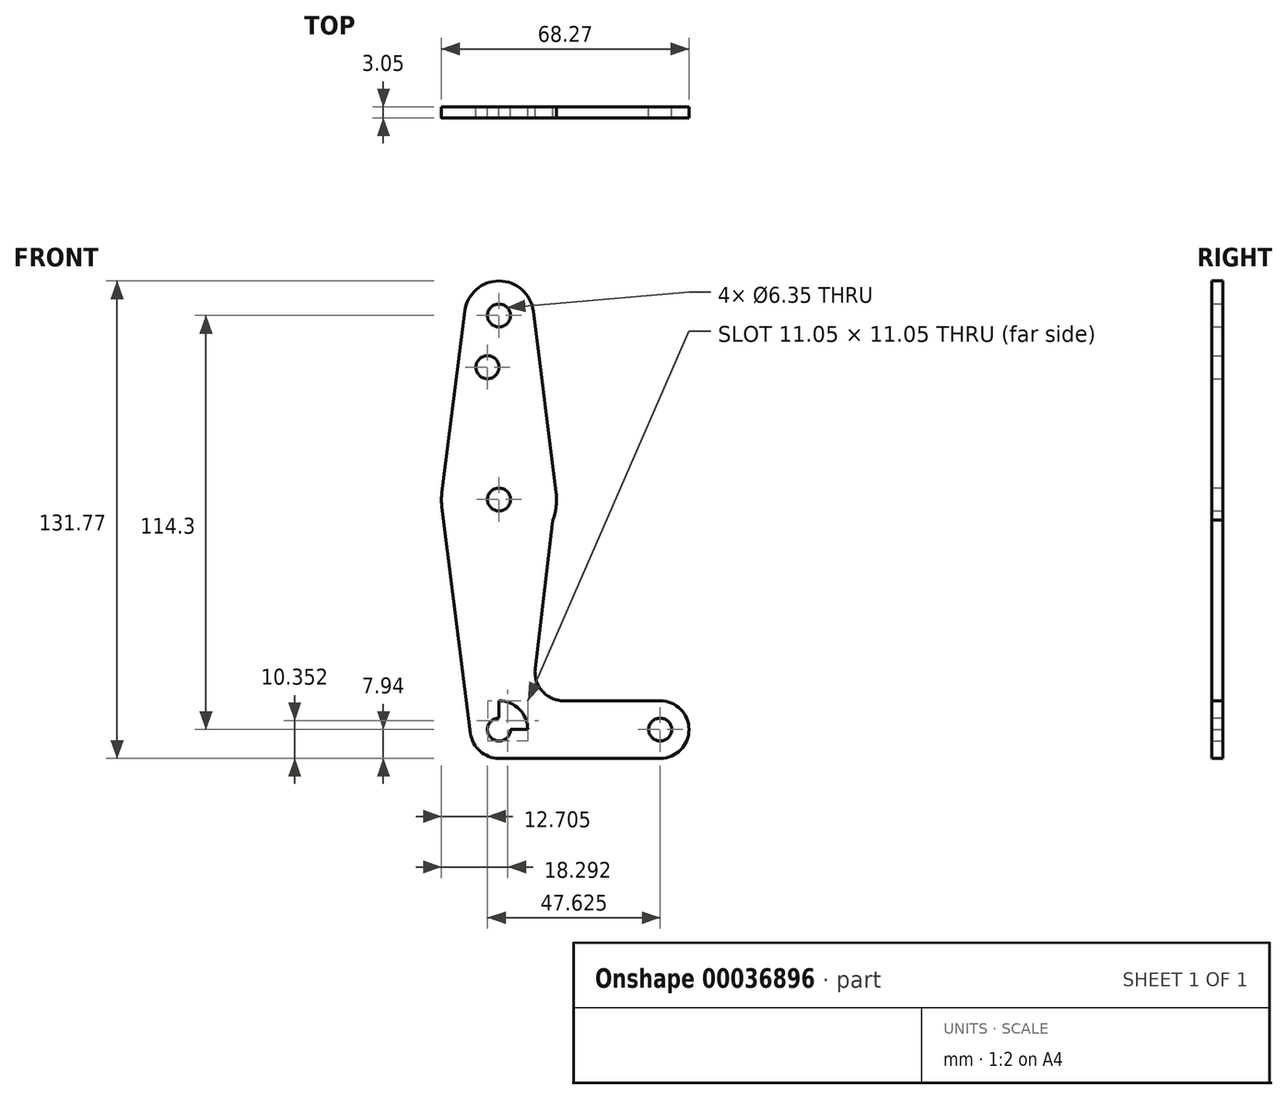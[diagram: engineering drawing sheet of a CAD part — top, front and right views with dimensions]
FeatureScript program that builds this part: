
annotation { "Feature Type Name" : "Feature", "Feature Type Description" : "" }
export const myFeature = defineFeature(function(context is Context, id is Id, definition is map)
    precondition{}
    {
        {
            var Q0;
            Q0=qCreatedBy(makeId("Front.planeOp"),FACE);
            var sketch = newSketch(context, id + "F0", { "sketchPlane" : qUnion([Q0])});
            skCircle(sketch, "E0", {"center": v(0, 0) * mm, "radius": 7.94 * mm});
            skCircle(sketch, "E1", {"center": v(0, 63.5) * mm, "radius": 15.88 * mm});
            skCircle(sketch, "E2", {"center": v(0, 114.3) * mm, "radius": 9.53 * mm});
            skCircle(sketch, "E3", {"center": v(44.45, 0) * mm, "radius": 7.94 * mm});
            skLineSegment(sketch, "E4", {"start": v(0, 114.3) * mm, "end": v(0, 0) * mm});
            skLineSegment(sketch, "E5", {"start": v(0, 0) * mm, "end": v(44.45, 0) * mm});
            skLineSegment(sketch, "E6", {"start": v(0, 63.5) * mm, "end": v(0, 0) * mm});
            skLineSegment(sketch, "E7", {"start": v(0, -7.94) * mm, "end": v(44.45, -7.94) * mm});
            skLineSegment(sketch, "E8", {"start": v(17.88, 7.94) * mm, "end": v(44.45, 7.94) * mm});
            skLineSegment(sketch, "E9", {"start": v(-9.45, 115.5) * mm, "end": v(-15.75, 65.48) * mm});
            skLineSegment(sketch, "E10", {"start": v(9.45, 115.5) * mm, "end": v(15.75, 65.48) * mm});
            skLineSegment(sketch, "E11", {"start": v(15.75, 65.48) * mm, "end": v(9.99, 16.82) * mm});
            skCircle(sketch, "E12", {"center": v(0, 114.3) * mm, "radius": 0.32 * mm});
            skCircle(sketch, "E13", {"center": v(-3.17, 100.03) * mm, "radius": 3.18 * mm});
            skCircle(sketch, "E14", {"center": v(0, 63.5) * mm, "radius": 3.17 * mm});
            skCircle(sketch, "E15", {"center": v(0, 0) * mm, "radius": 3.18 * mm});
            skCircle(sketch, "E16", {"center": v(44.45, 0) * mm, "radius": 3.18 * mm});
            skCircle(sketch, "E17", {"center": v(0, 114.3) * mm, "radius": 3.18 * mm});
            skArc(sketch, "E18.filletArc", {"start": v(9.99, 16.82) * mm, "mid": v(11.94, 10.6) * mm, "end": v(17.88, 7.94) * mm});
            skLineSegment(sketch, "E19", {"start": v(-15.73, 61.37) * mm, "end": v(-7.88, -1) * mm});
            skSolve(sketch);
        }
        {
            var Q0;
            Q0 = qSketchRegion(id + "F0", true);
            var Q1;
            {var subQ0=sQuery(id+"F0.wireOp",EDGE,"E6");var subQ3=sQuery(id+"F0.wireOp",EDGE,"E0");var subQ4=makeQuery(id+"F0.imprint","INTERSECT",VERTEX,{"derivedFrom":[subQ3,subQ0]});Q1=makeQuery(id+"F0.imprint","IMPRINT",FACE,{"disambiguationData":[TD([[makeQuery(id+"F0.imprint","IMPRINT",EDGE,{"disambiguationData":[TD([[subQ4,1.0]])],"derivedFrom":subQ3}),1.0]])]});}
            extrude(context, id + "F1", {"entities" : qUnion([Q0, Q1]), "depth" : 3.05 * mm});
        }
    });
